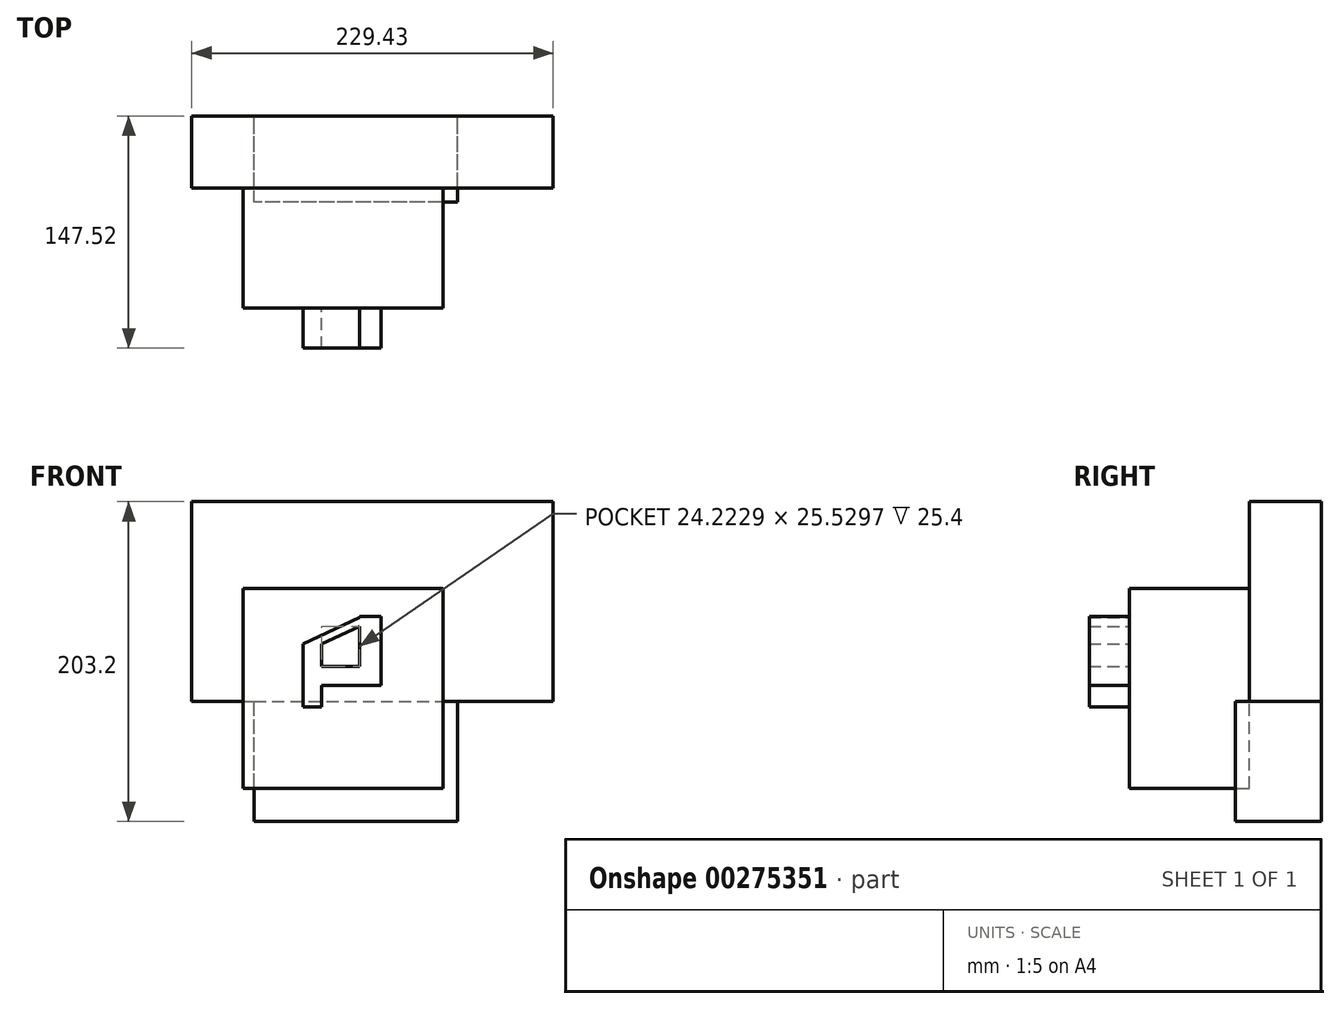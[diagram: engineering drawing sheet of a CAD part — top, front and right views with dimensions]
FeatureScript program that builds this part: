
annotation { "Feature Type Name" : "Feature", "Feature Type Description" : "" }
export const myFeature = defineFeature(function(context is Context, id is Id, definition is map)
    precondition{}
    {
        {
            var Q0;
            Q0=qCreatedBy(makeId("Front.planeOp"),FACE);
            var sketch = newSketch(context, id + "F0", { "sketchPlane" : qUnion([Q0])});
            skLineSegment(sketch, "E0.bottom", {"start": v(-65.62, 71.96) * mm, "end": v(61.38, 71.96) * mm});
            skLineSegment(sketch, "E0.top", {"start": v(-65.62, -55.04) * mm, "end": v(61.38, -55.04) * mm});
            skLineSegment(sketch, "E0.left", {"start": v(-65.62, 71.96) * mm, "end": v(-65.62, -55.04) * mm});
            skLineSegment(sketch, "E0.right", {"start": v(61.38, 71.96) * mm, "end": v(61.38, -55.04) * mm});
            skSolve(sketch);
        }
        {
            var Q0;
            Q0 = qSketchRegion(id + "F0", true);
            extrude(context, id + "F1", {"entities" : qUnion([Q0]), "depth" : 76.2 * mm});
        }
        {
            var Q0;
            Q0=qCreatedBy(makeId("Top.planeOp"),FACE);
            var sketch = newSketch(context, id + "F2", { "sketchPlane" : qUnion([Q0])});
            skLineSegment(sketch, "E1.bottom", {"start": v(-98.33, 0) * mm, "end": v(131.1, 0) * mm});
            skLineSegment(sketch, "E1.top", {"start": v(-98.33, 45.78) * mm, "end": v(131.1, 45.78) * mm});
            skLineSegment(sketch, "E1.left", {"start": v(-98.33, 0) * mm, "end": v(-98.33, 45.78) * mm});
            skLineSegment(sketch, "E1.right", {"start": v(131.1, 0) * mm, "end": v(131.1, 45.78) * mm});
            skSolve(sketch);
        }
        {
            var Q0;
            Q0 = qSketchRegion(id + "F2", true);
            extrude(context, id + "F3", {"entities" : qUnion([Q0]), "operationType" : NewBodyOperationType.ADD, "depth" : 127 * mm});
        }
        {
            var Q0;
            Q0=qCreatedBy(makeId("Top.planeOp"),FACE);
            var sketch = newSketch(context, id + "F4", { "sketchPlane" : qUnion([Q0])});
            skLineSegment(sketch, "E2.bottom", {"start": v(70.55, -8.95) * mm, "end": v(-58.72, -8.95) * mm});
            skLineSegment(sketch, "E2.top", {"start": v(70.55, 45.92) * mm, "end": v(-58.72, 45.92) * mm});
            skLineSegment(sketch, "E2.left", {"start": v(70.55, -8.95) * mm, "end": v(70.55, 45.92) * mm});
            skLineSegment(sketch, "E2.right", {"start": v(-58.72, -8.95) * mm, "end": v(-58.72, 45.92) * mm});
            skSolve(sketch);
        }
        {
            var Q0;
            Q0 = qSketchRegion(id + "F4", true);
            extrude(context, id + "F5", {"entities" : qUnion([Q0]), "operationType" : NewBodyOperationType.ADD, "oppositeDirection" : true, "depth" : 76.2 * mm});
        }
        {
            var Q0;
            Q0=qCreatedBy(makeId("Front.planeOp"),FACE);
            var sketch = newSketch(context, id + "F6", { "sketchPlane" : qUnion([Q0])});
            skLineSegment(sketch, "E3.bottom", {"start": v(-27.58, 36.52) * mm, "end": v(-15.97, 36.52) * mm});
            skLineSegment(sketch, "E3.top", {"start": v(-27.58, -3.3) * mm, "end": v(-15.97, -3.3) * mm});
            skLineSegment(sketch, "E3.left", {"start": v(-27.58, 36.52) * mm, "end": v(-27.58, -3.3) * mm});
            skLineSegment(sketch, "E3.right", {"start": v(-15.97, 36.52) * mm, "end": v(-15.97, -3.3) * mm});
            skLineSegment(sketch, "E4.bottom", {"start": v(-15.97, 22.25) * mm, "end": v(8.26, 22.25) * mm});
            skLineSegment(sketch, "E4.top", {"start": v(-15.97, 10.3) * mm, "end": v(8.26, 10.3) * mm});
            skLineSegment(sketch, "E4.left", {"start": v(-15.97, 22.25) * mm, "end": v(-15.97, 10.3) * mm});
            skLineSegment(sketch, "E4.right", {"start": v(8.26, 22.25) * mm, "end": v(8.26, 10.3) * mm});
            skLineSegment(sketch, "E5.bottom", {"start": v(8.26, 10.3) * mm, "end": v(21.86, 10.3) * mm});
            skLineSegment(sketch, "E5.top", {"start": v(8.26, 54.1) * mm, "end": v(21.86, 54.1) * mm});
            skLineSegment(sketch, "E5.left", {"start": v(8.26, 10.3) * mm, "end": v(8.26, 54.1) * mm});
            skLineSegment(sketch, "E5.right", {"start": v(21.86, 10.3) * mm, "end": v(21.86, 54.1) * mm});
            skLineSegment(sketch, "E6", {"start": v(21.86, 54.1) * mm, "end": v(-15.97, 36.52) * mm});
            skLineSegment(sketch, "E7", {"start": v(8.92, 53.77) * mm, "end": v(-27.58, 36.52) * mm});
            skSolve(sketch);
        }
        {
            var Q0;
            Q0 = qSketchRegion(id + "F6", true);
            extrude(context, id + "F7", {"entities" : qUnion([Q0]), "operationType" : NewBodyOperationType.ADD, "depth" : 101.6 * mm});
        }
    });
